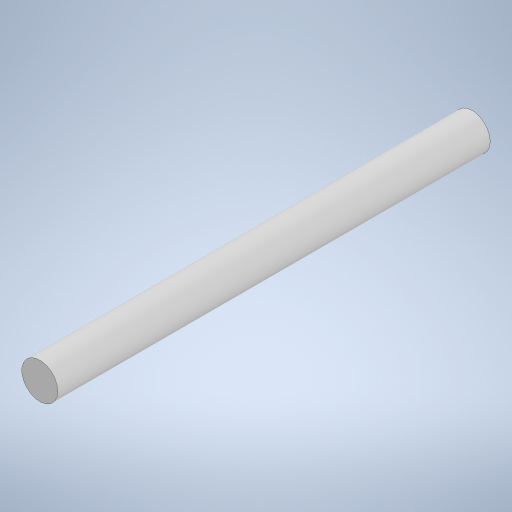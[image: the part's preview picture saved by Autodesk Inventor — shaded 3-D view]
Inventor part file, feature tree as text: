
AUTODESK INVENTOR PART (.ipt)
format: ipt  version: 2023 (Build 270158000, 158)  size: 227,840 bytes
history: native  units: in
note: dims shown in document units (in); Inventor stores cm internally (conversion verified against a paired STEP export)
features: extrude x1, sketch x1
ambient origin geometry x8: Origin, YZ Plane, XZ Plane, XY Plane, X Axis, Y Axis, Z Axis, Center Point
bodies: Solid1 (feature_tree)
feature tree (2):
  extrude  "Extrusion1"  Depth=27.0in TaperAngle=0.0deg
  sketch  "Sketch1"  dims[d0=2.25in d1=27.0in d2=0.0in]
